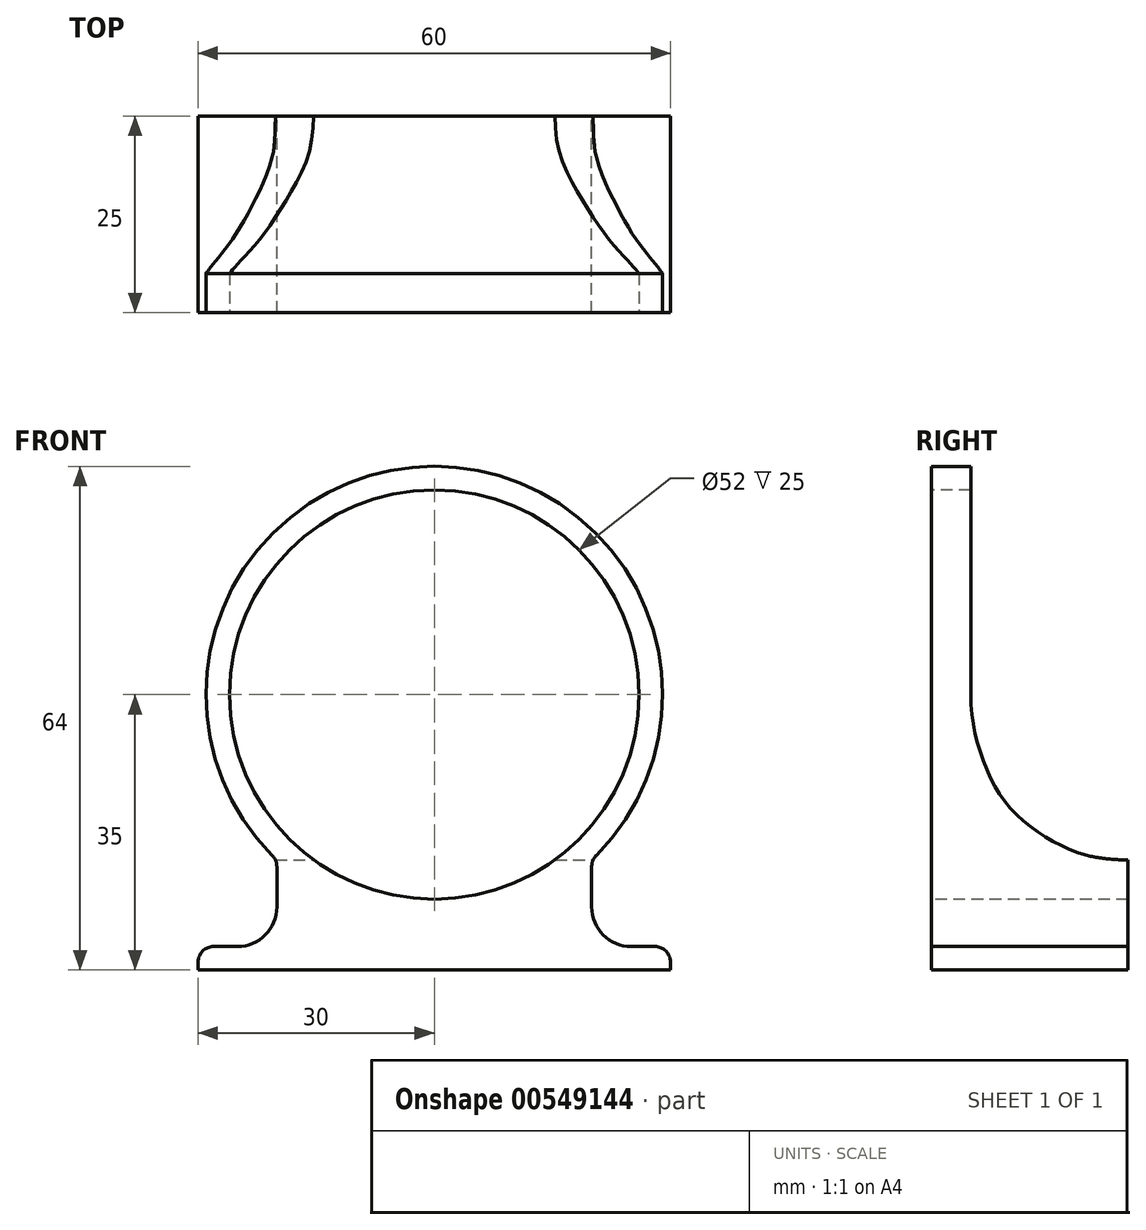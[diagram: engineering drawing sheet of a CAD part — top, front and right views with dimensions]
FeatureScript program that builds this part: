
annotation { "Feature Type Name" : "Feature", "Feature Type Description" : "" }
export const myFeature = defineFeature(function(context is Context, id is Id, definition is map)
    precondition{}
    {
        {
            var Q0;
            Q0=qCreatedBy(makeId("Front.planeOp"),FACE);
            var sketch = newSketch(context, id + "F0", { "sketchPlane" : qUnion([Q0])});
            skCircle(sketch, "E0", {"center": v(0, 0) * mm, "radius": 26 * mm});
            skCircle(sketch, "E1", {"center": v(0, 0) * mm, "radius": 29 * mm});
            skSolve(sketch);
        }
        {
            var Q0;
            Q0 = qSketchRegion(id + "F0", true);
            extrude(context, id + "F1", {"entities" : qUnion([Q0]), "oppositeDirection" : true, "depth" : 25 * mm, "offsetDistance" : 25 * mm});
        }
        {
            var Q0;
            Q0=makeQuery(id+"F1.opExtrude","CAP_FACE",FACE,{"disambiguationData":[OSD([sQuery(id+"F0.wireOp",EDGE,"E0"),sQuery(id+"F0.wireOp",EDGE,"E1")])],"isStart":true});
            var sketch = newSketch(context, id + "F2", { "sketchPlane" : qUnion([Q0])});
            skLineSegment(sketch, "E2", {"start": v(-20, -16.61) * mm, "end": v(-20, -32) * mm});
            skLineSegment(sketch, "E3", {"start": v(-20, -32) * mm, "end": v(-30, -32) * mm});
            skLineSegment(sketch, "E4", {"start": v(-30, -32) * mm, "end": v(-30, -35) * mm});
            skLineSegment(sketch, "E5", {"start": v(-30, -35) * mm, "end": v(30, -35) * mm});
            skLineSegment(sketch, "E6", {"start": v(30, -35) * mm, "end": v(30, -32) * mm});
            skLineSegment(sketch, "E7", {"start": v(30, -32) * mm, "end": v(20, -32) * mm});
            skLineSegment(sketch, "E8", {"start": v(20, -32) * mm, "end": v(20, -16.61) * mm});
            skPoint(sketch, "E9.0.center.orphan", {"position": v(0, 0) * mm});
            skArc(sketch, "E10.0", {"start": v(-20, -16.61) * mm, "mid": v(0, -26) * mm, "end": v(20, -16.61) * mm});
            skSolve(sketch);
        }
        {
            var Q0;
            Q0 = qSketchRegion(id + "F2", true);
            extrude(context, id + "F3", {"entities" : qUnion([Q0]), "operationType" : NewBodyOperationType.ADD, "oppositeDirection" : true, "depth" : 25 * mm, "offsetDistance" : 25 * mm});
        }
        {
            var Q0;
            Q0=makeQuery(id+"F3.opExtrude","SWEPT_EDGE",EDGE,{"disambiguationData":[OSD([sQuery(id+"F2.wireOp",EDGE,"E7"),sQuery(id+"F2.wireOp",EDGE,"E8")])]});
            var Q1;
            Q1=makeQuery(id+"F3.opExtrude","SWEPT_EDGE",EDGE,{"disambiguationData":[OSD([sQuery(id+"F2.wireOp",EDGE,"E2"),sQuery(id+"F2.wireOp",EDGE,"E3")])]});
            fillet(context, id + "F4", {"entities" : qUnion([Q0, Q1]), "radius" : 5 * mm, "tangentPropagation" : true, "allowEdgeOverflow" : false});
        }
        {
            var Q0;
            Q0=qCreatedBy(makeId("Right.planeOp"),FACE);
            var sketch = newSketch(context, id + "F5", { "sketchPlane" : qUnion([Q0])});
            skLineSegment(sketch, "E11", {"start": v(5, 29) * mm, "end": v(5, -19.95) * mm, "construction": true});
            skLineSegment(sketch, "E12", {"start": v(0, 0) * mm, "end": v(28.99, 0) * mm, "construction": true});
            skLineSegment(sketch, "E13.0", {"start": v(25, -21) * mm, "end": v(0, -21) * mm, "construction": true});
            skFitSpline(sketch, "E14", {"points": [v(25, -21) * mm, v(15.3, -18.54) * mm, v(8.82, -12.86) * mm, v(5.48, -4.53) * mm, v(5, 0) * mm], "startDerivative": vector(-48.76, 0) * mm, "endDerivative": vector(0, 23.29) * mm});
            skLineSegment(sketch, "E15", {"start": v(5, 0) * mm, "end": v(5, 29) * mm});
            skLineSegment(sketch, "E16", {"start": v(5, 29) * mm, "end": v(30.63, 29) * mm});
            skLineSegment(sketch, "E17", {"start": v(30.63, 29) * mm, "end": v(25, -21) * mm});
            skSolve(sketch);
        }
        {
            var Q0;
            Q0=makeQuery(id+"F5.imprint","IMPRINT",FACE,{"disambiguationData":[TD([[makeQuery(id+"F5.imprint","IMPRINT",EDGE,{"derivedFrom":sQuery(id+"F5.wireOp",EDGE,"E14")}),-1.0]])]});
            extrude(context, id + "F6", {"entities" : qUnion([Q0]), "operationType" : NewBodyOperationType.REMOVE, "endBound" : BoundingType.THROUGH_ALL, "oppositeDirection" : true, "depth" : 25 * mm, "offsetDistance" : 25 * mm, "hasSecondDirection" : true, "secondDirectionBound" : SecondDirectionBoundingType.THROUGH_ALL, "secondDirectionOppositeDirection" : false, "secondDirectionDepth" : 25 * mm});
        }
        {
            var Q0;
            Q0=makeQuery(id+"F3.boolean.opBoolean","INTERSECT",EDGE,{"derivedFrom":[makeQuery(id+"F1.opExtrude","SWEPT_FACE",FACE,{"disambiguationData":[OSD([sQuery(id+"F0.wireOp",EDGE,"E1")])]}),makeQuery(id+"F3.opExtrude","SWEPT_FACE",FACE,{"disambiguationData":[OSD([sQuery(id+"F2.wireOp",EDGE,"E8")])]})]});
            var Q1;
            Q1=makeQuery(id+"F3.boolean.opBoolean","INTERSECT",EDGE,{"derivedFrom":[makeQuery(id+"F1.opExtrude","SWEPT_FACE",FACE,{"disambiguationData":[OSD([sQuery(id+"F0.wireOp",EDGE,"E1")])]}),makeQuery(id+"F3.opExtrude","SWEPT_FACE",FACE,{"disambiguationData":[OSD([sQuery(id+"F2.wireOp",EDGE,"E2")])]})]});
            var Q2;
            {var subQ0=sQuery(id+"F2.wireOp",EDGE,"E2");var subQ3=sQuery(id+"F5.wireOp",EDGE,"E14");Q2=makeQuery(id+"F6.boolean.opBoolean","COPY",EDGE,{"disambiguationData":[TD([makeQuery(id+"F3.opExtrude","SWEPT_FACE",FACE,{"disambiguationData":[OSD([subQ0])]})])],"derivedFrom":makeQuery(id+"F6.opExtrude","SWEPT_EDGE",EDGE,{"disambiguationData":[OSD([subQ3,sQuery(id+"F5.wireOp",EDGE,"E17")])]})});}
            var Q3;
            {var subQ1=sQuery(id+"F2.wireOp",EDGE,"E8");var subQ3=sQuery(id+"F5.wireOp",EDGE,"E14");Q3=makeQuery(id+"F6.boolean.opBoolean","COPY",EDGE,{"disambiguationData":[TD([makeQuery(id+"F3.opExtrude","SWEPT_FACE",FACE,{"disambiguationData":[OSD([subQ1])]})])],"derivedFrom":makeQuery(id+"F6.opExtrude","SWEPT_EDGE",EDGE,{"disambiguationData":[OSD([subQ3,sQuery(id+"F5.wireOp",EDGE,"E17")])]})});}
            fillet(context, id + "F7", {"entities" : qUnion([Q0, Q1, Q2, Q3]), "radius" : 2 * mm, "tangentPropagation" : true, "allowEdgeOverflow" : false});
        }
        {
            var Q0;
            Q0=makeQuery(id+"F3.opExtrude","SWEPT_EDGE",EDGE,{"disambiguationData":[OSD([sQuery(id+"F2.wireOp",EDGE,"E6"),sQuery(id+"F2.wireOp",EDGE,"E7")])]});
            var Q1;
            Q1=makeQuery(id+"F3.opExtrude","SWEPT_EDGE",EDGE,{"disambiguationData":[OSD([sQuery(id+"F2.wireOp",EDGE,"E3"),sQuery(id+"F2.wireOp",EDGE,"E4")])]});
            fillet(context, id + "F8", {"entities" : qUnion([Q0, Q1]), "radius" : 2 * mm, "tangentPropagation" : true, "allowEdgeOverflow" : false});
        }
    });
